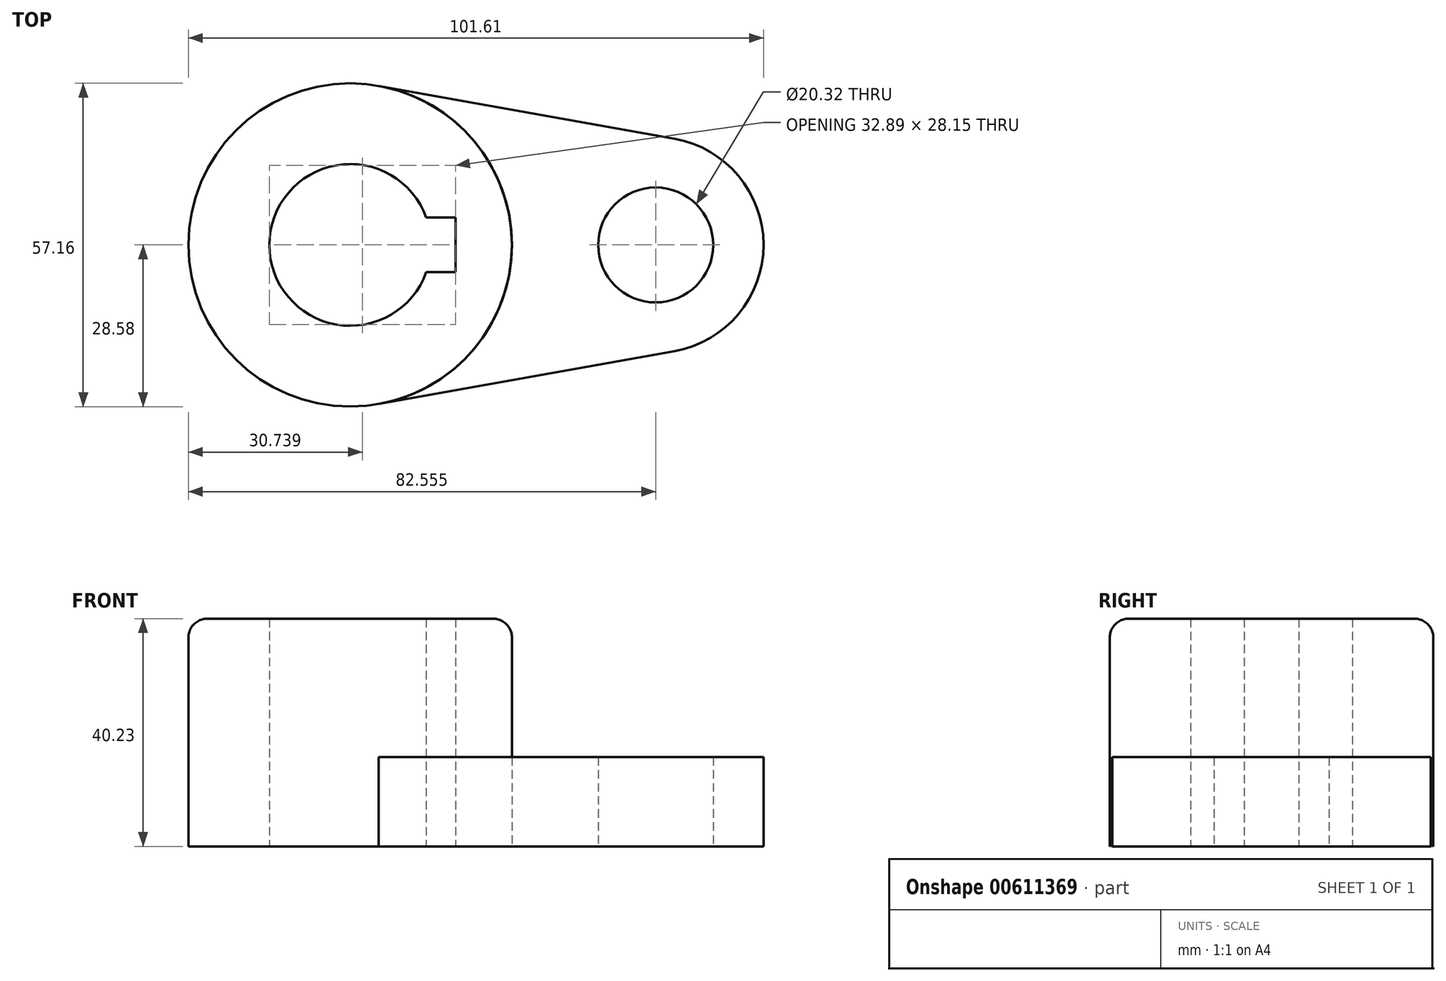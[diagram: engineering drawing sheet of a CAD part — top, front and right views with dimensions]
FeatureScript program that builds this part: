
annotation { "Feature Type Name" : "Feature", "Feature Type Description" : "" }
export const myFeature = defineFeature(function(context is Context, id is Id, definition is map)
    precondition{}
    {
        {
            var Q0;
            Q0=qCreatedBy(makeId("Top.planeOp"),FACE);
            var sketch = newSketch(context, id + "F0", { "sketchPlane" : qUnion([Q0])});
            skCircle(sketch, "E0", {"center": v(0, 0) * mm, "radius": 28.58 * mm});
            skCircle(sketch, "E1", {"center": v(0, 0) * mm, "radius": 14.29 * mm});
            skCircle(sketch, "E2", {"center": v(53.98, 0) * mm, "radius": 10.16 * mm});
            skArc(sketch, "E3", {"start": v(57.34, -18.75) * mm, "mid": v(73.03, 0) * mm, "end": v(57.34, 18.75) * mm});
            skLineSegment(sketch, "E4", {"start": v(57.34, 18.75) * mm, "end": v(5.04, 28.13) * mm});
            skLineSegment(sketch, "E5", {"start": v(57.34, -18.75) * mm, "end": v(5.04, -28.13) * mm});
            skLineSegment(sketch, "E6.bottom", {"start": v(18.6, 4.83) * mm, "end": v(-18.6, 4.83) * mm});
            skLineSegment(sketch, "E6.top", {"start": v(18.6, -4.83) * mm, "end": v(-18.6, -4.83) * mm});
            skLineSegment(sketch, "E6.left", {"start": v(18.6, 4.83) * mm, "end": v(18.6, -4.83) * mm});
            skLineSegment(sketch, "E6.right", {"start": v(-18.6, 4.83) * mm, "end": v(-18.6, -4.83) * mm});
            skSolve(sketch);
        }
        {
            var Q0;
            {var subQ8=sQuery(id+"F0.wireOp",EDGE,"E6.left");Q0=makeQuery(id+"F0.imprint","IMPRINT",FACE,{"disambiguationData":[TD([[makeQuery(id+"F0.imprint","IMPRINT",EDGE,{"derivedFrom":subQ8}),1.0]])]});}
            var Q1;
            {var subQ5=sQuery(id+"F0.wireOp",EDGE,"E6.right");Q1=makeQuery(id+"F0.imprint","IMPRINT",FACE,{"disambiguationData":[TD([[makeQuery(id+"F0.imprint","IMPRINT",EDGE,{"derivedFrom":subQ5}),1.0]])]});}
            extrude(context, id + "F1", {"entities" : qUnion([Q0, Q1]), "depth" : 40.23 * mm, "offsetDistance" : 25.4 * mm});
        }
        {
            var Q0;
            Q0=makeQuery(id+"F0.imprint","IMPRINT",FACE,{"disambiguationData":[TD([[makeQuery(id+"F0.imprint","IMPRINT",EDGE,{"derivedFrom":sQuery(id+"F0.wireOp",EDGE,"E2")}),-1.0]])]});
            extrude(context, id + "F2", {"entities" : qUnion([Q0]), "depth" : 15.77 * mm, "offsetDistance" : 25.4 * mm});
        }
        {
            var Q0;
            Q0=makeQuery(id+"F1.opExtrude","CAP_EDGE",EDGE,{"disambiguationData":[OSD([sQuery(id+"F0.wireOp",EDGE,"E0")])],"isStart":false});
            fillet(context, id + "F3", {"entities" : qUnion([Q0]), "radius" : 3.3 * mm, "tangentPropagation" : true, "allowEdgeOverflow" : false});
        }
    });
